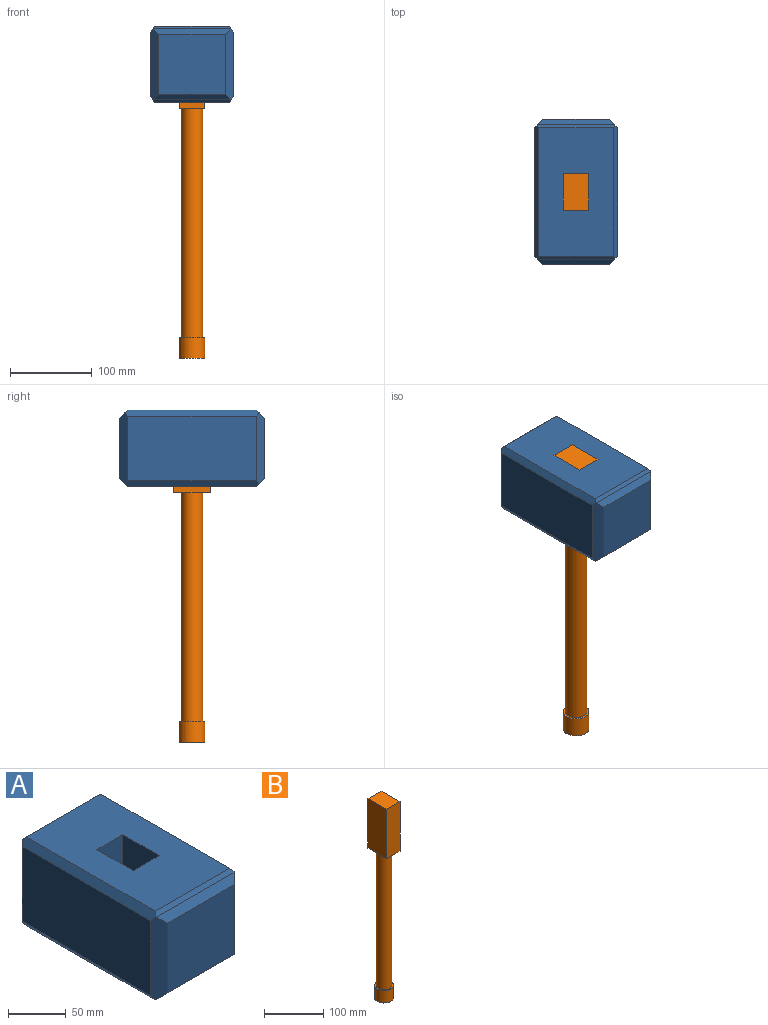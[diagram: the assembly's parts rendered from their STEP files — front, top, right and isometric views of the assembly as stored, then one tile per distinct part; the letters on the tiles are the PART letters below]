
ASSEMBLY  parts=2 mates=1
PART A: 26 faces, bbox 101.6x177.8x94 mm
  f0: plane 156.97x90.72mm, normal (0,0,1), area 12829.5mm2, adj f18,f19,f20,f21,f22,f23,f24,f25
  f1: plane 156.97x90.72mm, normal (0,0,-1), area 12829.5mm2, adj f14,f15,f16,f17,f22,f23,f24,f25
  f2: plane 81.28x73.66mm, normal (0,-1,0), area 5987.1mm2, adj f6,f7,f8,f9
  f3: plane 157.48x79.1mm, normal (1,0,0), area 12457.2mm2, adj f7,f11,f14,f18
  f4: plane 81.28x73.66mm, normal (0,1,0), area 5987.1mm2, adj f10,f11,f12,f13
  f5: plane 157.48x79.1mm, normal (-1,0,0), area 12457.2mm2, adj f8,f12,f17,f21
  f6: plane 94.42x6.57mm, normal (0,-0.71,-0.71), area 816mm2, adj f2,f7,f8,f15
  f7: plane 87.66x10.16mm, normal (0.71,-0.71,0), area 1171.3mm2, adj f2,f3,f6,f9,f14,f15,f18,f19
  f8: plane 87.66x10.16mm, normal (-0.71,-0.71,0), area 1171.3mm2, adj f2,f5,f6,f9,f15,f17,f19,f21
  f9: plane 94.42x6.57mm, normal (0,-0.71,0.71), area 816mm2, adj f2,f7,f8,f19
  f10: plane 94.42x6.57mm, normal (0,0.71,-0.71), area 816mm2, adj f4,f11,f12,f16
  f11: plane 87.66x10.16mm, normal (0.71,0.71,0), area 1171.3mm2, adj f3,f4,f10,f13,f14,f16,f18,f20
  f12: plane 87.66x10.16mm, normal (-0.71,0.71,0), area 1171.3mm2, adj f4,f5,f10,f13,f16,f17,f20,f21
  f13: plane 94.42x6.57mm, normal (0,0.71,0.71), area 816mm2, adj f4,f11,f12,f20
  f14: plane 163.74x7.44mm, normal (0.81,0,-0.59), area 1479mm2, adj f1,f3,f7,f11,f15,f16
  f15: plane 95.34x3.85mm, normal (0,-0.68,-0.73), area 490.8mm2, adj f1,f6,f7,f8,f14,f17
  f16: plane 95.34x3.85mm, normal (0,0.68,-0.73), area 490.8mm2, adj f1,f10,f11,f12,f14,f17
  f17: plane 163.74x7.44mm, normal (-0.81,0,-0.59), area 1479mm2, adj f1,f5,f8,f12,f15,f16
  f18: plane 163.74x7.44mm, normal (0.81,0,0.59), area 1479mm2, adj f0,f3,f7,f11,f19,f20
  f19: plane 95.34x3.85mm, normal (0,-0.68,0.73), area 490.8mm2, adj f0,f7,f8,f9,f18,f21
  f20: plane 95.34x3.85mm, normal (0,0.68,0.73), area 490.8mm2, adj f0,f11,f12,f13,f18,f21
  f21: plane 163.74x7.44mm, normal (-0.81,0,0.59), area 1479mm2, adj f0,f5,f8,f12,f19,f20
  f22: plane 93.98x31.75mm, normal (0,-1,0), area 2983.9mm2, adj f0,f1,f23,f25
  f23: plane 93.98x44.45mm, normal (-1,0,0), area 4177.4mm2, adj f0,f1,f22,f24
  f24: plane 93.98x31.75mm, normal (0,1,0), area 2983.9mm2, adj f0,f1,f23,f25
  f25: plane 93.98x44.45mm, normal (1,0,0), area 4177.4mm2, adj f0,f1,f22,f24
PART B: 10 faces, bbox 31.8x44.5x406.4 mm
  f0: plane 101.6x31.75mm, normal (0,-1,0), area 3225.8mm2, adj f1,f3,f4,f5
  f1: plane 101.6x44.45mm, normal (1,0,0), area 4516.1mm2, adj f0,f2,f4,f5
  f2: plane 101.6x31.75mm, normal (0,1,0), area 3225.8mm2, adj f1,f3,f4,f5
  f3: plane 101.6x44.45mm, normal (-1,0,0), area 4516.1mm2, adj f0,f2,f4,f5
  f4: plane 44.45x31.75mm, normal (0,0,1), area 1411.3mm2, adj f0,f1,f2,f3
  f5: plane 44.45x31.75mm, normal (0,0,-1), area 859.8mm2, adj f0,f1,f2,f3,f6
  f6: cylinder r=13.25mm len=279.4mm, axis (0,0,1), area 23259.7mm2, adj f5,f9
  f7: cylinder r=15.88mm len=31.75mm, axis (0,0,1), area 2533.5mm2, adj f8,f9
  f8: plane 31.75x31.75mm, normal (0,0,-1), area 791.7mm2, adj f7
  f9: plane 31.75x31.75mm, normal (0,0,1), area 240.2mm2, adj f6,f7
PLACE A t=(6.91,-46.05,129.7)mm
PLACE B t=(6.91,-46.05,122.08)mm
MATE planar A.f0 <-> B.f6  axis (0,0,1) through (6.91,-46.05,223.68)mm
